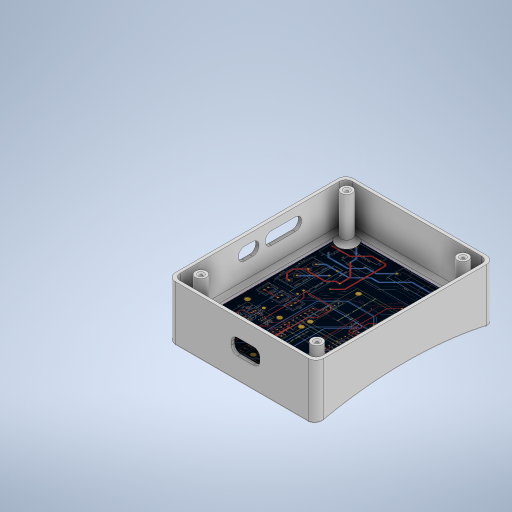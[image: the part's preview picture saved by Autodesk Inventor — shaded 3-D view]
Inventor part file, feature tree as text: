
AUTODESK INVENTOR PART (.ipt)
format: ipt  version: 2024.4 (Build 284460000, 460)  size: 1,006,592 bytes
history: native  units: mm
features: sketch x9, fillet x9, extrude x8, other x1
ambient origin geometry x8: Origin, YZ Plane, XZ Plane, XY Plane, X Axis, Y Axis, Z Axis, Center Point
bodies: Solid1 (feature_tree)
feature tree (27):
  sketch  "Sketch1"  dims[d28=4.0mm d29=2.0mm]
  extrude  "Extrusion1"  Depth=2.0mm
  extrude  "Extrusion2"  Depth=2.0mm
  extrude  "Extrusion3"  Depth=2.0mm TaperAngle=0.0deg
  extrude  "Extrusion4"  Depth=7.0mm
  fillet  "Fillet4"  Radius=7.0mm
  fillet  "Fillet5"  Radius=7.0mm
  extrude  "Extrusion5"  Depth=2.0mm
  extrude  "Extrusion6"  Depth=2.0mm
  fillet  "Fillet6"  Radius=2.0mm
  fillet  "Fillet7"  Radius=12.0mm
  fillet  "Fillet8"  Radius=3.0mm
  extrude  "Extrusion7"  Depth=7.0mm TaperAngle=0.0deg
  fillet  "Fillet10"  Radius=112.838mm
  fillet  "Fillet11"  Radius=240.0mm
  extrude  "Extrusion8"  Depth=5.0mm
  fillet  "Fillet12"  Radius=4.0mm
  fillet  "Fillet13"  Radius=5.0mm
  other  "Image3"
  sketch  "Sketch2"  dims[d30=4.0mm d31=2.0mm]
  sketch  "Sketch3"  dims[d32=26.5mm d33=0.0mm d34=2.0mm d35=0.0mm]
  sketch  "Sketch4"  dims[d38=7.0mm d39=7.0mm d40=7.0mm d41=7.0mm]
  sketch  "Sketch5"  dims[d42=28.0mm d43=0.0mm d45=2.0mm]
  sketch  "Sketch6"  dims[d46=2.0mm d47=2.0mm d48=2.0mm d49=12.0mm d50=0.0mm d51=3.0mm]
  sketch  "Sketch7"  dims[d52=2.3mm d53=7.0mm d54=0.0mm d56=112.838mm d57=240.0mm]
  sketch  "Sketch8"  dims[d58=20.0mm d59=0.0mm d60=5.0mm d61=4.0mm d62=5.0mm]
  sketch  "Sketch9"  dims[d63=5.0mm d64=5.0mm d65=5.0mm d66=1.0mm d67=15.0mm d68=0.0mm d70=8.0mm d71=40.0mm d72=3.0mm d73=4.0mm d74=25.0mm d76=4.0mm d80=13.0mm d81=23.0mm d82=26.5mm d83=0.0mm d84=4.0mm d85=10.0mm d86=18.0mm d87=40.5mm d90=12.5mm d91=1.0mm d92=7.0mm d93=7.0mm d23=0.5mm d24=0.872665mm d25=0.5mm d26=0.872665mm d77=0.5mm d78=0.872665mm d79=0.5mm]
